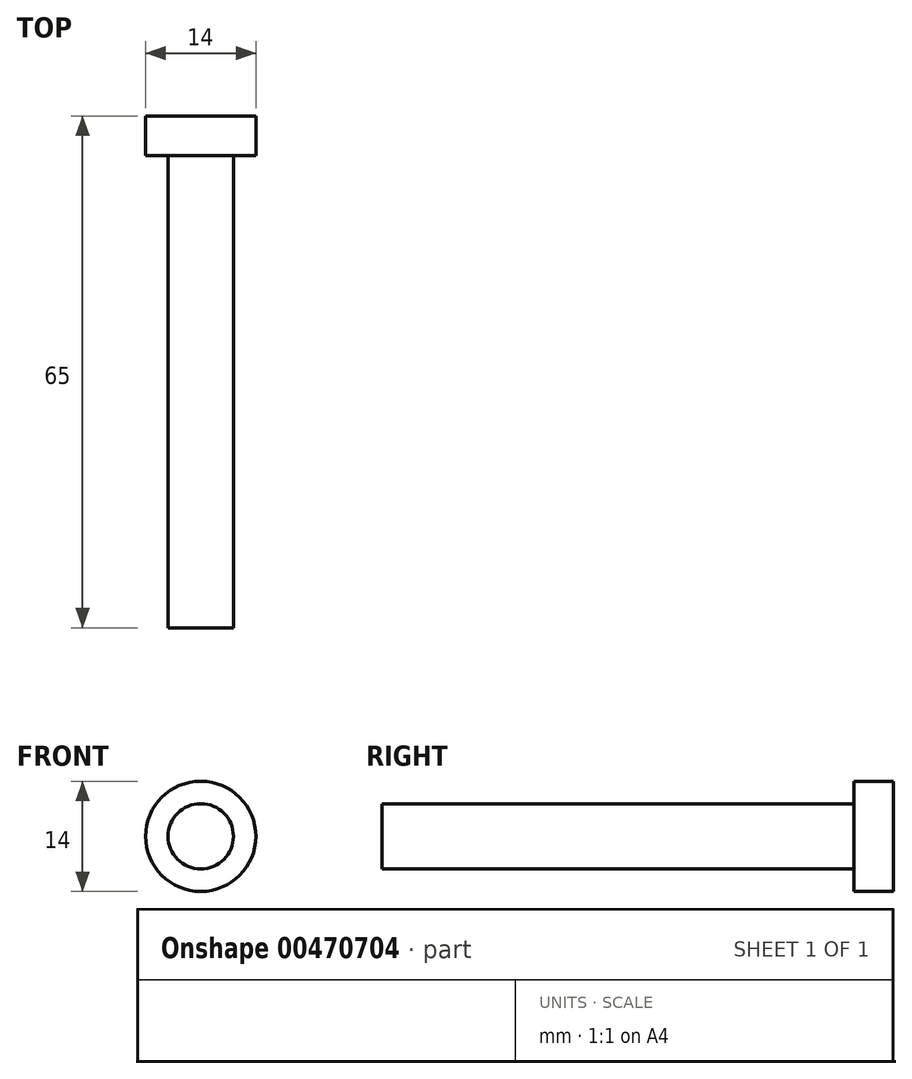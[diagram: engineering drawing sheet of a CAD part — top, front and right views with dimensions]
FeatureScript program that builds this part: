
annotation { "Feature Type Name" : "Feature", "Feature Type Description" : "" }
export const myFeature = defineFeature(function(context is Context, id is Id, definition is map)
    precondition{}
    {
        {
            var Q0;
            Q0=qCreatedBy(makeId("Front.planeOp"),FACE);
            var sketch = newSketch(context, id + "F0", { "sketchPlane" : qUnion([Q0])});
            skCircle(sketch, "E0", {"center": v(0, 0) * mm, "radius": 4.15 * mm});
            skCircle(sketch, "E1", {"center": v(0, 0) * mm, "radius": 7 * mm});
            skSolve(sketch);
        }
        {
            var Q0;
            Q0=makeQuery(id+"F0.imprint","IMPRINT",FACE,{"disambiguationData":[TD([[makeQuery(id+"F0.imprint","IMPRINT",EDGE,{"derivedFrom":sQuery(id+"F0.wireOp",EDGE,"E0")}),1.0]])]});
            extrude(context, id + "F1", {"entities" : qUnion([Q0]), "depth" : 60 * mm});
        }
        {
            var Q0;
            Q0 = qSketchRegion(id + "F0", true);
            var Q1;
            Q1=makeQuery(id+"F1.opExtrude","CAP_FACE",FACE,{"disambiguationData":[OSD([sQuery(id+"F0.wireOp",EDGE,"E0")])],"isStart":true});
            extrude(context, id + "F2", {"entities" : qUnion([Q0, Q1]), "operationType" : NewBodyOperationType.ADD, "oppositeDirection" : true, "depth" : 5 * mm});
        }
    });
